# Revit family: CENTUM Festpunkt Typ B m XL100 Massivanschluss, Ø139,7 bis Ø457 Gummi_
name_source: partatom
category: HLS-Bauteile
revit_build: Autodesk Revit 2018 (Build: 20190510_1515(x64)
units: mm (PartAtom-declared; Revit-internal decimal feet)

## family parameters
Arbeitsebenenbasiert = Ja
Beim Laden mit Abzugskörper schneiden = Nein
Bemaßung runder Anschluss = Durchmesser verwenden
Gemeinsam genutzt = Ja
Immer vertikal = Nein
Klassifizierung = Keine
Raumberechnungspunkt = Nein
Teiletyp = Normal

## types (8) — shared parameters
Anzahl Rohrschellen = 2
Breite Material Rohrschelle = 50 mm
Fabrikat = MEFA
Kurztext1 = Festpunkt Typ B
Länge Druckstück = 116 mm
Material Druckstücke = Stahl
Materialname Druckstücke = S235JR
Mengeneinheit = St
Oberfläche Druckstücke = blank
Oberfläche Träger + Schellen = galvanisch verzinkt
Rohrschellentyp = Titan HD
Schalldämmeinlage = Gummi TPE/EPDM
Stärke Material Rohrschelle = 5 mm
Vorgabe-Ansicht = 1219 mm
max. Temperaturbeständigkeit = 100 °C
vpe = 1
zero-valued in all types: max. Höhe

## per-type parameters (varying)
| type | Artikelnummer | Aufbaumaß | Breite | Breite Profilstahl | EAN | Festpunkt Typ B | Gewicht | Gewicht pro Bauteil | Höhe Profilstahl | Klammergröße | Kurztext2 | Länge Profilstahl | Profilstahltyp | Rohraußendurchmesser | max. Axiale Reaktionskraft | max. Rohraußendurchmesser | min. Rohraußendurchmesser |
| CENTUM Festpunkt Typ B, Ø 139,7mm, m. XL100 Massivanschluss, Gummi | 9991612 | 69 mm | 231 mm  [stored 0.757874 ft] | 80 mm | 4250928454287 | Festpunkt Typ B m.XL100 Massivanschluss Ø139,7mm, Gummi_1 : CENTUM Festpunkt Typ B, Ø139,7, m. XL100 Massivanschluss, Gummi | 12.44 kg | 12.44 kg | 45 mm | 2 | 139,7 mm Gummi | 200 mm  [stored 0.656168 ft] | U80 | 140 mm | 40 kN | 0 mm  [stored 0 ft] | 0 mm  [stored 0 ft] |
| CENTUM Festpunkt Typ B, Ø 168,3mm, m. XL100 Massivanschluss, Gummi | 9993874 | 79 mm | 258 mm  [stored 0.846457 ft] | 120 mm | 4250928454294 | Festpunkt Typ B m.XL100 Massivanschluss Ø168 bis 457mm, Gummi_1 : CENTUM Festpunkt Typ B, Ø 168,3, m. XL100 Massivanschluss, Gummi | 20.15 kg | 20.15 kg | 55 mm |  | 168,3 mm Gummi | 330 mm  [stored 1.08268 ft] | U120 | 168 mm  [stored 0.551181 ft] | 60 kN | 0 mm  [stored 0 ft] | 0 mm  [stored 0 ft] |
| CENTUM Festpunkt Typ B, Ø 219,1mm, m. XL100 Massivanschluss, Gummi | 9994028 | 79 mm | 309 mm  [stored 1.01378 ft] | 120 mm | 4250928454300 | Festpunkt Typ B m.XL100 Massivanschluss Ø168 bis 457mm, Gummi_1 : CENTUM Festpunkt Typ B, Ø 219,1, m. XL100 Massivanschluss, Gummi | 20.91 kg | 20.91 kg | 55 mm |  | 219,1 mm Gummi | 330 mm  [stored 1.08268 ft] | U120 | 219 mm  [stored 0.718504 ft] | 60 kN | 0 mm  [stored 0 ft] | 0 mm  [stored 0 ft] |
| CENTUM Festpunkt Typ B, Ø 273-274, m. XL100 Massivanschluss, Gummi | 9994029 | 79 mm | 363 mm  [stored 1.19094 ft] | 120 mm | 4250928454317 | Festpunkt Typ B m.XL100 Massivanschluss Ø168 bis 457mm, Gummi_1 : CENTUM Festpunkt Typ B, Ø 273-274, m. XL100 Massivanschluss, Gummi | 21.72 kg | 21.72 kg | 55 mm |  | 273 - 274 mm Gummi | 330 mm  [stored 1.08268 ft] | U120 | 0 mm  [stored 0 ft] | 60 kN | 274 mm  [stored 0.89895 ft] | 273 mm  [stored 0.895669 ft] |
| CENTUM Festpunkt Typ B, Ø 323,9mm, m. XL100 Massivanschluss, Gummi | 9993005 | 79 mm | 414 mm  [stored 1.35827 ft] | 120 mm | 4250928454324 | Festpunkt Typ B m.XL100 Massivanschluss Ø168 bis 457mm, Gummi_1 : CENTUM Festpunkt Typ B, Ø 323,9, m. XL100 Massivanschluss, Gummi | 22.49 kg | 22.49 kg | 55 mm |  | 323,9 mm Gummi | 330 mm  [stored 1.08268 ft] | U120 | 324 mm | 60 kN | 0 mm  [stored 0 ft] | 0 mm  [stored 0 ft] |
| CENTUM Festpunkt Typ B, Ø 355-356mm, m. XL100 Massivanschluss, Gummi | 9993146 | 79 mm | 446 mm  [stored 1.46325 ft] | 120 mm | 4250928454331 | Festpunkt Typ B m.XL100 Massivanschluss Ø168 bis 457mm, Gummi_1 : CENTUM Festpunkt Typ B, Ø 355-356, m. XL100 Massivanschluss, Gummi | 22.95 kg | 22.95 kg | 55 mm |  | 355 - 356 mm Gummi | 330 mm  [stored 1.08268 ft] | U120 | 0 mm  [stored 0 ft] | 60 kN | 356 mm  [stored 1.16798 ft] | 355 mm |
| CENTUM Festpunkt Typ B, Ø 406,4mm, m. XL100 Massivanschluss, Gummi | 9993006 | 79 mm | 498 mm  [stored 1.63386 ft] | 120 mm | 4250928454348 | Festpunkt Typ B m.XL100 Massivanschluss Ø168 bis 457mm, Gummi_1 : CENTUM Festpunkt Typ B, Ø 406,4mm, m. XL100 Massivanschluss, Gummi | 23.72 kg | 23.72 kg | 55 mm |  | 406,4 mm Gummi | 330 mm  [stored 1.08268 ft] | U120 | 406 mm | 60 kN | 0 mm  [stored 0 ft] | 0 mm  [stored 0 ft] |
| CENTUM Festpunkt Typ B, Ø 457mm, m. XL100 Massivanschluss, Gummi | 9993145 | 79 mm | 549 mm  [stored 1.80118 ft] | 120 mm | 4250928454355 | Festpunkt Typ B m.XL100 Massivanschluss Ø168 bis 457mm, Gummi_1 : CENTUM Festpunkt Typ B, Ø 457, m. XL100 Massivanschluss, Gummi | 24.48 kg | 24.48 kg | 55 mm |  | 457 mm Gummi | 330 mm  [stored 1.08268 ft] | U120 | 457 mm  [stored 1.49934 ft] | 60 kN | 0 mm  [stored 0 ft] | 0 mm  [stored 0 ft] |

note: [stored X ft] marks values corroborated as IEEE doubles in the binary element streams (Revit-internal decimal feet)

## geometry (parser evidence)
native form markers: Sweep x11
no freeform markers — native parametric forms only
